# Revit family: Lighting-ArredoUrbano-GEWISS-URBAN[O3]-LED-INNESTO_LATERALE_OTTICA_ELLITTICA
name_source: partatom
category: Apparecchi per illuminazione
units: mm (PartAtom-declared; Revit-internal decimal feet)

## family parameters
Condiviso = No
Host = Superficie
Numero OmniClass = 23.80.70.00
Punto di calcolo locali = Sì
Quota connettore circolare = Usa diametro
Sorgente d'illuminazione = No
Taglio con vuoti quando caricato = No
Tipo di parte = Normale
Titolo OmniClass = Lighting

## types (1)
- Lighting-ArredoUrbano-GEWISS-URBAN[O3]-LED-INNESTO_LATERALE_OTTICA_ELLITTICA
    Adatto per = Sbracci commerciali ad innesto laterale
    Adatto per: = Sbracci commerciali ad innesto laterale
    Applicazione = Esterno
    Catalogo = LIGHTING
    Catalogo Serie = URBAN [O3]
    Classe isolamento = II
    Codice EAN = 8011564803022
    Codice Electrocod = 244C
    Colore = Grigio grafite
    Corrente di pilotaggio = 530mA
    Corrente di pilotaggio LED = 530mA
    Descrizione = URBAN LED 4M 4000K BIREGIME INNESTO LAT. OTTICA ELLITTICA GRIGIO
    Distanza minima dall'oggetto illuminato = 1M
    Finitura = GEWISS - GRIGIO GRAFITE
    Flusso nominale (lm) = 13400
    Funzionalità alimentatore = Biregime
    Garanzia = 5 anni
    Grado di protezione = IP66
    IDF = 5ffb71a5-d642-42b0-a96d-c68381e7dd14
    IDT = da31b83e-a88b-4408-9115-206c2dedd00b
    Immagine tipo = GWS7251.jpg
    LED Life time (L80B10) = 100000H
    LED LifeTime (L80B20) = 50000h
    LED LifeTime (L90B20) = 50000H
    Lumen output (lm) = 11240
    Modello = GWS7278
    N. moduli Chorus = 4 (4x16 LED)
    Numero moduli = 4 (4x16 LED)
    Ottica = Ellittica - ULOR: 0%
    Peso (kg) = 11
    Peso (kg): = 11
    Potenza di sistema = 105W
    Produttore = GEWISS S.p.A.
    Prospetto di default = 1219 mm
    Resistenza agli urti = IK08 CORPO - IK06 LENTI
    Rischio fotobiologico = RG1/RG2 @ 20cm
    Rischio fotobiologico: = RG1/RG2 @ 20cm
    SEO = Stradale
    Scheda Tecnica = https://www.gewiss.com
    Superficie massima esposta al vento = 0,25M2
    Temperatura di colore = 4000 K (CRI 70)
    Temperatura di colore: = 4000 K (CRI 70)
    Temperatura di funzionamento = -25 +35 °C
    Temperatura di utilizzo = -25 +35 °C
    Tensione = 220/240 V - 50/60 Hz - Biregime con autoapprendimento
    Tensione: = 220/240 V - 50/60 Hz
    Tipo alimentatore = Driver Led in corrente continua
    Tipologia lampada = LED
    Tipologia sorgente luminosa = LED
    URL = https://www.gewiss.com
    Versione file RFA = 20.11
    Vetro = GEWISS - VETRO

## geometry (parser evidence)
native form markers: Blend x4
no freeform markers — native parametric forms only
